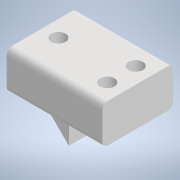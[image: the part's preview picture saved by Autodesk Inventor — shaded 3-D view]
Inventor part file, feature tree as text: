
AUTODESK INVENTOR PART (.ipt)
format: ipt  version: 2020.2 (Build 242310000, 310)  size: 170,496 bytes
history: native  units: mm
features: fillet x5, sketch x4, extrude x3, hole x2
ambient origin geometry x8: Origin, YZ Plane, XZ Plane, XY Plane, X Axis, Y Axis, Z Axis, Center Point
bodies: Solido1 (feature_tree)
feature tree (14):
  extrude  "Estrusione1"  Depth=35.0mm
  hole  "Foro1"  [1 undecoded]
  fillet  "Raccordo1"  Radius=19.0mm
  fillet  "Raccordo2"  Radius=8.0mm
  fillet  "Raccordo3"  [1 undecoded]
  fillet  "Raccordo4"  Radius=3.0mm
  hole  "Foro2"  [1 undecoded]
  extrude  "Estrusione2"  Depth=3.0mm
  extrude  "Estrusione3"  Depth=3.0mm
  fillet  "Raccordo5"  Radius=7.0mm
  sketch  "Schizzo1"
  sketch  "Schizzo3"
  sketch  "Schizzo4"
  sketch  "Schizzo5"
note: 3 required parameter values undecoded (feature->parameter linkage not recoverable at this tier; creation-order binding heuristic only, values carry confidence <= 0.55)
